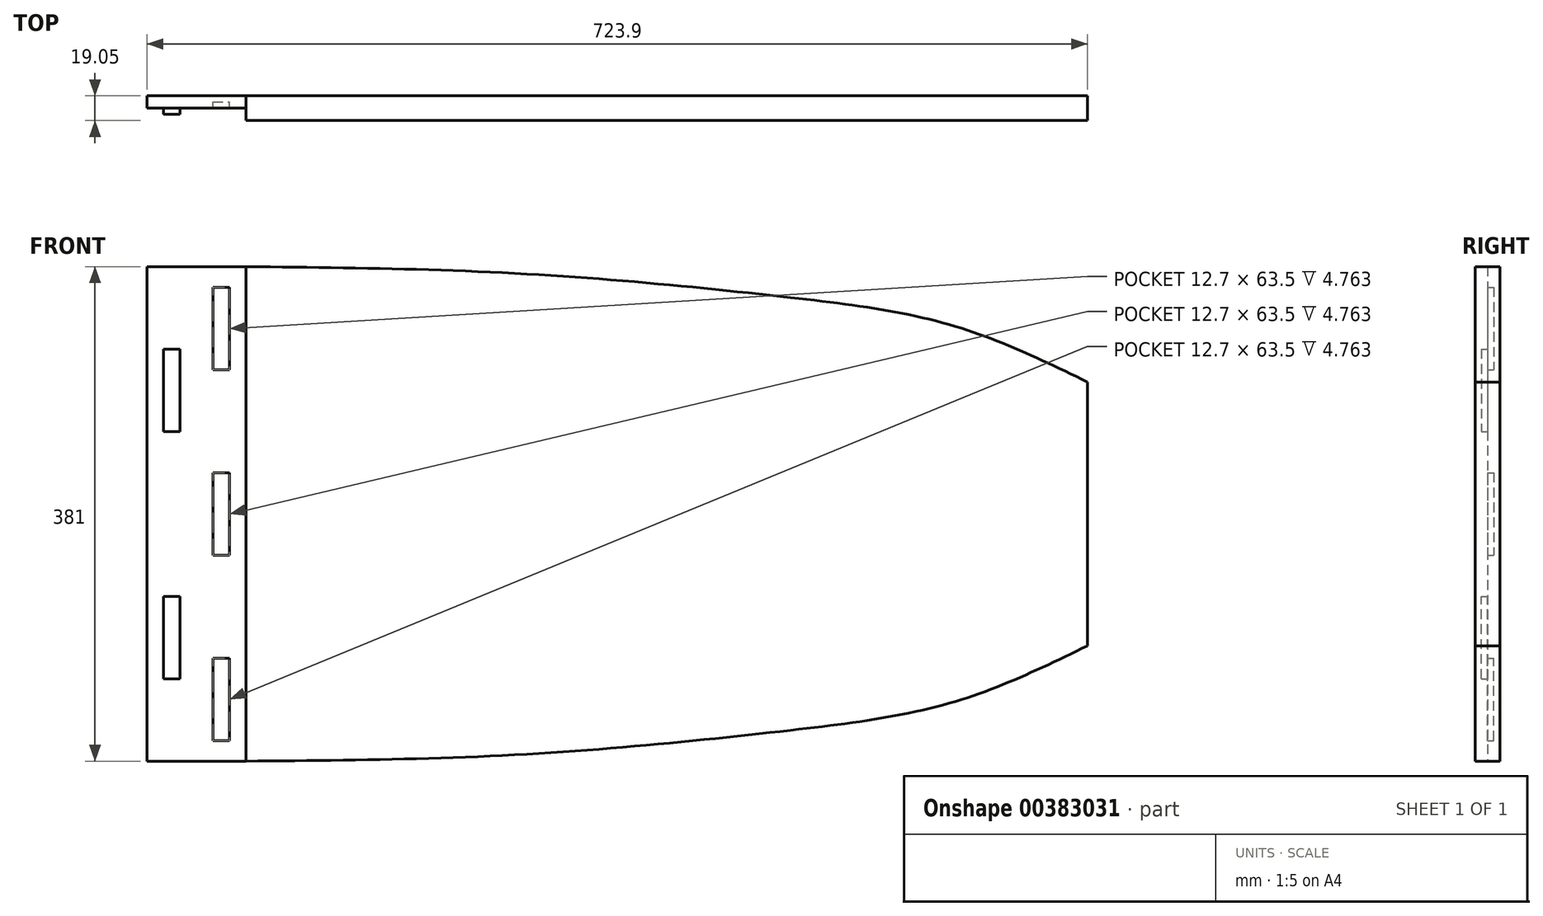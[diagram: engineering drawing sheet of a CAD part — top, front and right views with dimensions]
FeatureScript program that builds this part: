
annotation { "Feature Type Name" : "Feature", "Feature Type Description" : "" }
export const myFeature = defineFeature(function(context is Context, id is Id, definition is map)
    precondition{}
    {
        {
            var Q0;
            Q0=qCreatedBy(makeId("Front.planeOp"),FACE);
            var sketch = newSketch(context, id + "F0", { "sketchPlane" : qUnion([Q0])});
            skLineSegment(sketch, "E0.MirrorCS", {"start": v(-123.27, -13.78) * mm, "end": v(-123.27, 176.72) * mm});
            skLineSegment(sketch, "E1.MirrorCS", {"start": v(169.25, -13.9) * mm, "end": v(169.25, 171.04) * mm});
            skLineSegment(sketch, "E2.MirrorCS", {"start": v(372.03, -13.78) * mm, "end": v(372.03, 152.9) * mm});
            skLineSegment(sketch, "E3.MirrorCS", {"start": v(499.03, -13.78) * mm, "end": v(499.03, 130.68) * mm});
            skLineSegment(sketch, "E4.MirrorCS", {"start": v(600.63, -13.78) * mm, "end": v(600.63, 87.82) * mm});
            skLineSegment(sketch, "E5.MirrorCS", {"start": v(600.63, -13.78) * mm, "end": v(600.63, -115.38) * mm});
            skLineSegment(sketch, "E6.MirrorCS", {"start": v(499.03, -13.78) * mm, "end": v(499.03, -158.24) * mm});
            skLineSegment(sketch, "E7.MirrorCS", {"start": v(372.03, -13.78) * mm, "end": v(372.03, -180.47) * mm});
            skLineSegment(sketch, "E8.MirrorCS", {"start": v(169.25, -13.9) * mm, "end": v(169.25, -198.85) * mm});
            skLineSegment(sketch, "E9", {"start": v(-123.27, -13.78) * mm, "end": v(-104.22, -13.78) * mm});
            skLineSegment(sketch, "E10", {"start": v(-104.22, -13.78) * mm, "end": v(-104.22, 176.72) * mm});
            skLineSegment(sketch, "E11", {"start": v(-104.22, 176.72) * mm, "end": v(-104.22, 81.47) * mm});
            skLineSegment(sketch, "E12.bottom", {"start": v(-110.57, 113.22) * mm, "end": v(-97.87, 113.22) * mm});
            skLineSegment(sketch, "E12.top", {"start": v(-110.57, 49.72) * mm, "end": v(-97.87, 49.72) * mm});
            skLineSegment(sketch, "E12.left", {"start": v(-110.57, 113.22) * mm, "end": v(-110.57, 49.72) * mm});
            skLineSegment(sketch, "E12.right", {"start": v(-97.87, 113.22) * mm, "end": v(-97.87, 49.72) * mm});
            skPoint(sketch, "E12.middle", {"position": v(-104.22, 81.47) * mm});
            skLineSegment(sketch, "E13", {"start": v(-104.22, -13.78) * mm, "end": v(-85.17, -13.78) * mm});
            skLineSegment(sketch, "E14", {"start": v(-123.27, 176.72) * mm, "end": v(-85.17, 176.72) * mm});
            skLineSegment(sketch, "E15", {"start": v(-85.17, -13.78) * mm, "end": v(-85.17, 176.72) * mm});
            skLineSegment(sketch, "E16", {"start": v(-85.17, 176.72) * mm, "end": v(-47.07, 176.72) * mm});
            skLineSegment(sketch, "E17", {"start": v(-47.07, 176.72) * mm, "end": v(-47.07, -13.78) * mm});
            skLineSegment(sketch, "E18", {"start": v(-85.17, -13.78) * mm, "end": v(-47.07, -13.78) * mm});
            skLineSegment(sketch, "E19", {"start": v(-85.17, -13.78) * mm, "end": v(-66.12, -13.78) * mm});
            skLineSegment(sketch, "E20", {"start": v(-66.12, -13.78) * mm, "end": v(-66.12, 176.72) * mm});
            skLineSegment(sketch, "E21", {"start": v(-66.12, -13.78) * mm, "end": v(-66.12, 81.47) * mm});
            skLineSegment(sketch, "E22", {"start": v(-66.12, 176.72) * mm, "end": v(-66.12, 81.47) * mm});
            skLineSegment(sketch, "E23", {"start": v(-66.12, 129.1) * mm, "end": v(-66.12, 176.72) * mm});
            skLineSegment(sketch, "E24.bottom", {"start": v(-72.47, 160.84) * mm, "end": v(-59.77, 160.84) * mm});
            skLineSegment(sketch, "E24.top", {"start": v(-72.47, 97.34) * mm, "end": v(-59.77, 97.34) * mm});
            skLineSegment(sketch, "E24.left", {"start": v(-72.47, 160.84) * mm, "end": v(-72.47, 97.34) * mm});
            skLineSegment(sketch, "E24.right", {"start": v(-59.77, 160.84) * mm, "end": v(-59.77, 97.34) * mm});
            skPoint(sketch, "E24.middle", {"position": v(-66.12, 129.1) * mm});
            skLineSegment(sketch, "E25.bottom", {"start": v(-72.47, 17.97) * mm, "end": v(-59.77, 17.97) * mm});
            skLineSegment(sketch, "E25.top", {"start": v(-72.47, -45.53) * mm, "end": v(-59.77, -45.53) * mm});
            skLineSegment(sketch, "E25.left", {"start": v(-72.47, 17.97) * mm, "end": v(-72.47, -45.53) * mm});
            skLineSegment(sketch, "E25.right", {"start": v(-59.77, 17.97) * mm, "end": v(-59.77, -45.53) * mm});
            skPoint(sketch, "E25.middle", {"position": v(-66.12, -13.78) * mm});
            skLineSegment(sketch, "E26.MirrorCS", {"start": v(-123.27, -13.78) * mm, "end": v(-123.27, -204.28) * mm});
            skLineSegment(sketch, "E27.MirrorCS", {"start": v(-104.22, -13.78) * mm, "end": v(-104.22, -204.28) * mm});
            skLineSegment(sketch, "E28.MirrorCS", {"start": v(-85.17, -13.78) * mm, "end": v(-85.17, -204.28) * mm});
            skLineSegment(sketch, "E29.MirrorCS", {"start": v(-66.12, -13.78) * mm, "end": v(-66.12, -109.03) * mm});
            skLineSegment(sketch, "E30.MirrorCS", {"start": v(-47.07, -204.28) * mm, "end": v(-47.07, -13.78) * mm});
            skLineSegment(sketch, "E31.MirrorCS", {"start": v(-59.77, -45.53) * mm, "end": v(-59.77, 17.97) * mm});
            skLineSegment(sketch, "E32.MirrorCS", {"start": v(-97.87, -140.78) * mm, "end": v(-97.87, -77.28) * mm});
            skLineSegment(sketch, "E33.MirrorCS", {"start": v(-110.57, -140.78) * mm, "end": v(-110.57, -77.28) * mm});
            skLineSegment(sketch, "E34.MirrorCS", {"start": v(-110.57, -77.28) * mm, "end": v(-97.87, -77.28) * mm});
            skLineSegment(sketch, "E35.MirrorCS", {"start": v(-110.57, -140.78) * mm, "end": v(-97.87, -140.78) * mm});
            skLineSegment(sketch, "E36.MirrorCS", {"start": v(-72.47, -124.9) * mm, "end": v(-59.77, -124.9) * mm});
            skLineSegment(sketch, "E37.MirrorCS", {"start": v(-59.77, -188.4) * mm, "end": v(-59.77, -124.9) * mm});
            skLineSegment(sketch, "E38.MirrorCS", {"start": v(-72.47, -188.4) * mm, "end": v(-72.47, -124.9) * mm});
            skLineSegment(sketch, "E39.MirrorCS", {"start": v(-123.27, -204.28) * mm, "end": v(-85.17, -204.28) * mm});
            skLineSegment(sketch, "E40.MirrorCS", {"start": v(-85.17, -204.28) * mm, "end": v(-47.07, -204.28) * mm});
            skLineSegment(sketch, "E41.MirrorCS", {"start": v(-72.47, -188.4) * mm, "end": v(-59.77, -188.4) * mm});
            skFitSpline(sketch, "E42", {"points": [v(600.63, 87.82) * mm, v(499.03, 130.68) * mm, v(372.03, 152.9) * mm, v(169.25, 171.04) * mm, v(-47.07, 176.72) * mm], "startDerivative": vector(-481.19, 233.7) * mm, "endDerivative": vector(-743.56, 7.88) * mm});
            skFitSpline(sketch, "E43", {"points": [v(-47.07, -204.28) * mm, v(169.25, -198.85) * mm, v(372.03, -180.47) * mm, v(499.03, -158.24) * mm, v(600.63, -115.38) * mm], "startDerivative": vector(743.6, 6.47) * mm, "endDerivative": vector(481.19, 233.78) * mm});
            skSolve(sketch);
        }
        {
            var Q0;
            {var subQ3=sQuery(id+"F0.wireOp",EDGE,"E3.MirrorCS");Q0=makeQuery(id+"F0.imprint","IMPRINT",FACE,{"disambiguationData":[TD([[makeQuery(id+"F0.imprint","IMPRINT",EDGE,{"derivedFrom":subQ3}),-1.0]])]});}
            var Q1;
            {var subQ3=sQuery(id+"F0.wireOp",EDGE,"E1.MirrorCS");Q1=makeQuery(id+"F0.imprint","IMPRINT",FACE,{"disambiguationData":[TD([[makeQuery(id+"F0.imprint","IMPRINT",EDGE,{"derivedFrom":subQ3}),-1.0]])]});}
            var Q2;
            {var subQ2=sQuery(id+"F0.wireOp",EDGE,"E2.MirrorCS");Q2=makeQuery(id+"F0.imprint","IMPRINT",FACE,{"disambiguationData":[TD([[makeQuery(id+"F0.imprint","IMPRINT",EDGE,{"derivedFrom":subQ2}),-1.0]])]});}
            var Q3;
            {var subQ3=sQuery(id+"F0.wireOp",EDGE,"E1.MirrorCS");Q3=makeQuery(id+"F0.imprint","IMPRINT",FACE,{"disambiguationData":[TD([[makeQuery(id+"F0.imprint","IMPRINT",EDGE,{"derivedFrom":subQ3}),1.0]])]});}
            extrude(context, id + "F1", {"entities" : qUnion([Q0, Q1, Q2, Q3]), "depth" : 19.05 * mm});
        }
        {
            var Q0;
            {var subQ9=sQuery(id+"F0.wireOp",EDGE,"E0.MirrorCS");Q0=makeQuery(id+"F0.imprint","IMPRINT",FACE,{"disambiguationData":[TD([[makeQuery(id+"F0.imprint","IMPRINT",EDGE,{"derivedFrom":subQ9}),-1.0]])]});}
            var Q1;
            {var subQ0=sQuery(id+"F0.wireOp",EDGE,"E12.right");Q1=makeQuery(id+"F0.imprint","IMPRINT",FACE,{"disambiguationData":[TD([[makeQuery(id+"F0.imprint","IMPRINT",EDGE,{"derivedFrom":subQ0}),1.0]])]});}
            var Q2;
            {var subQ11=sQuery(id+"F0.wireOp",EDGE,"E15");Q2=makeQuery(id+"F0.imprint","IMPRINT",FACE,{"disambiguationData":[TD([[makeQuery(id+"F0.imprint","IMPRINT",EDGE,{"derivedFrom":subQ11}),-1.0]])]});}
            var Q3;
            {var subQ17=sQuery(id+"F0.wireOp",EDGE,"E17");Q3=makeQuery(id+"F0.imprint","IMPRINT",FACE,{"disambiguationData":[TD([[makeQuery(id+"F0.imprint","IMPRINT",EDGE,{"derivedFrom":subQ17}),-1.0]])]});}
            var Q4;
            {var subQ5=sQuery(id+"F0.wireOp",EDGE,"E9");Q4=makeQuery(id+"F0.imprint","IMPRINT",FACE,{"disambiguationData":[TD([[makeQuery(id+"F0.imprint","IMPRINT",EDGE,{"derivedFrom":subQ5}),-1.0]])]});}
            var Q5;
            {var subQ1=sQuery(id+"F0.wireOp",EDGE,"E13");Q5=makeQuery(id+"F0.imprint","IMPRINT",FACE,{"disambiguationData":[TD([[makeQuery(id+"F0.imprint","IMPRINT",EDGE,{"derivedFrom":subQ1}),-1.0]])]});}
            var Q6;
            {var subQ1=sQuery(id+"F0.wireOp",EDGE,"E28.MirrorCS");Q6=makeQuery(id+"F0.imprint","IMPRINT",FACE,{"disambiguationData":[TD([[makeQuery(id+"F0.imprint","IMPRINT",EDGE,{"derivedFrom":subQ1}),1.0]])]});}
            extrude(context, id + "F2", {"entities" : qUnion([Q0, Q1, Q2, Q3, Q4, Q5, Q6]), "operationType" : NewBodyOperationType.ADD, "depth" : 9.52 * mm});
        }
        {
            var Q0;
            Q0=makeQuery(id+"F0.imprint","IMPRINT",FACE,{"disambiguationData":[TD([[makeQuery(id+"F0.imprint","IMPRINT",EDGE,{"derivedFrom":sQuery(id+"F0.wireOp",EDGE,"E36.MirrorCS")}),-1.0]])]});
            var Q1;
            {var subQ3=sQuery(id+"F0.wireOp",EDGE,"E25.left");var subQ5=sQuery(id+"F0.wireOp",EDGE,"E25.top");var subQ6=makeQuery(id+"F0.imprint","INTERSECT",VERTEX,{"derivedFrom":[subQ5,subQ3]});Q1=makeQuery(id+"F0.imprint","IMPRINT",FACE,{"disambiguationData":[TD([[makeQuery(id+"F0.imprint","IMPRINT",EDGE,{"disambiguationData":[TD([[subQ6,-1.0]])],"derivedFrom":subQ5}),1.0]])]});}
            var Q2;
            {var subQ3=sQuery(id+"F0.wireOp",EDGE,"E31.MirrorCS");var subQ5=sQuery(id+"F0.wireOp",EDGE,"E25.top");var subQ6=makeQuery(id+"F0.imprint","INTERSECT",VERTEX,{"derivedFrom":[subQ5,subQ3]});Q2=makeQuery(id+"F0.imprint","IMPRINT",FACE,{"disambiguationData":[TD([[makeQuery(id+"F0.imprint","IMPRINT",EDGE,{"disambiguationData":[TD([[subQ6,1.0]])],"derivedFrom":subQ5}),1.0]])]});}
            var Q3;
            {var subQ3=sQuery(id+"F0.wireOp",EDGE,"E25.left");var subQ5=sQuery(id+"F0.wireOp",EDGE,"E25.bottom");var subQ7=makeQuery(id+"F0.imprint","INTERSECT",VERTEX,{"derivedFrom":[subQ5,subQ3]});Q3=makeQuery(id+"F0.imprint","IMPRINT",FACE,{"disambiguationData":[TD([[makeQuery(id+"F0.imprint","IMPRINT",EDGE,{"disambiguationData":[TD([[subQ7,-1.0]])],"derivedFrom":subQ5}),-1.0]])]});}
            var Q4;
            {var subQ3=sQuery(id+"F0.wireOp",EDGE,"E31.MirrorCS");var subQ5=sQuery(id+"F0.wireOp",EDGE,"E25.bottom");var subQ6=makeQuery(id+"F0.imprint","INTERSECT",VERTEX,{"derivedFrom":[subQ5,subQ3]});Q4=makeQuery(id+"F0.imprint","IMPRINT",FACE,{"disambiguationData":[TD([[makeQuery(id+"F0.imprint","IMPRINT",EDGE,{"disambiguationData":[TD([[subQ6,1.0]])],"derivedFrom":subQ5}),-1.0]])]});}
            var Q5;
            {var subQ0=sQuery(id+"F0.wireOp",EDGE,"E24.left");Q5=makeQuery(id+"F0.imprint","IMPRINT",FACE,{"disambiguationData":[TD([[makeQuery(id+"F0.imprint","IMPRINT",EDGE,{"derivedFrom":subQ0}),1.0]])]});}
            var Q6;
            {var subQ0=sQuery(id+"F0.wireOp",EDGE,"E24.right");Q6=makeQuery(id+"F0.imprint","IMPRINT",FACE,{"disambiguationData":[TD([[makeQuery(id+"F0.imprint","IMPRINT",EDGE,{"derivedFrom":subQ0}),-1.0]])]});}
            extrude(context, id + "F3", {"entities" : qUnion([Q0, Q1, Q2, Q3, Q4, Q5, Q6]), "operationType" : NewBodyOperationType.ADD, "depth" : 4.76 * mm});
        }
        {
            var Q0;
            {var subQ0=sQuery(id+"F0.wireOp",EDGE,"E12.right");Q0=makeQuery(id+"F0.imprint","IMPRINT",FACE,{"disambiguationData":[TD([[makeQuery(id+"F0.imprint","IMPRINT",EDGE,{"derivedFrom":subQ0}),-1.0]])]});}
            var Q1;
            {var subQ0=sQuery(id+"F0.wireOp",EDGE,"E12.left");Q1=makeQuery(id+"F0.imprint","IMPRINT",FACE,{"disambiguationData":[TD([[makeQuery(id+"F0.imprint","IMPRINT",EDGE,{"derivedFrom":subQ0}),1.0]])]});}
            var Q2;
            {var subQ5=sQuery(id+"F0.wireOp",EDGE,"E33.MirrorCS");Q2=makeQuery(id+"F0.imprint","IMPRINT",FACE,{"disambiguationData":[TD([[makeQuery(id+"F0.imprint","IMPRINT",EDGE,{"derivedFrom":subQ5}),-1.0]])]});}
            var Q3;
            {var subQ5=sQuery(id+"F0.wireOp",EDGE,"E32.MirrorCS");Q3=makeQuery(id+"F0.imprint","IMPRINT",FACE,{"disambiguationData":[TD([[makeQuery(id+"F0.imprint","IMPRINT",EDGE,{"derivedFrom":subQ5}),1.0]])]});}
            extrude(context, id + "F4", {"entities" : qUnion([Q0, Q1, Q2, Q3]), "operationType" : NewBodyOperationType.ADD, "depth" : 14.29 * mm});
        }
    });
